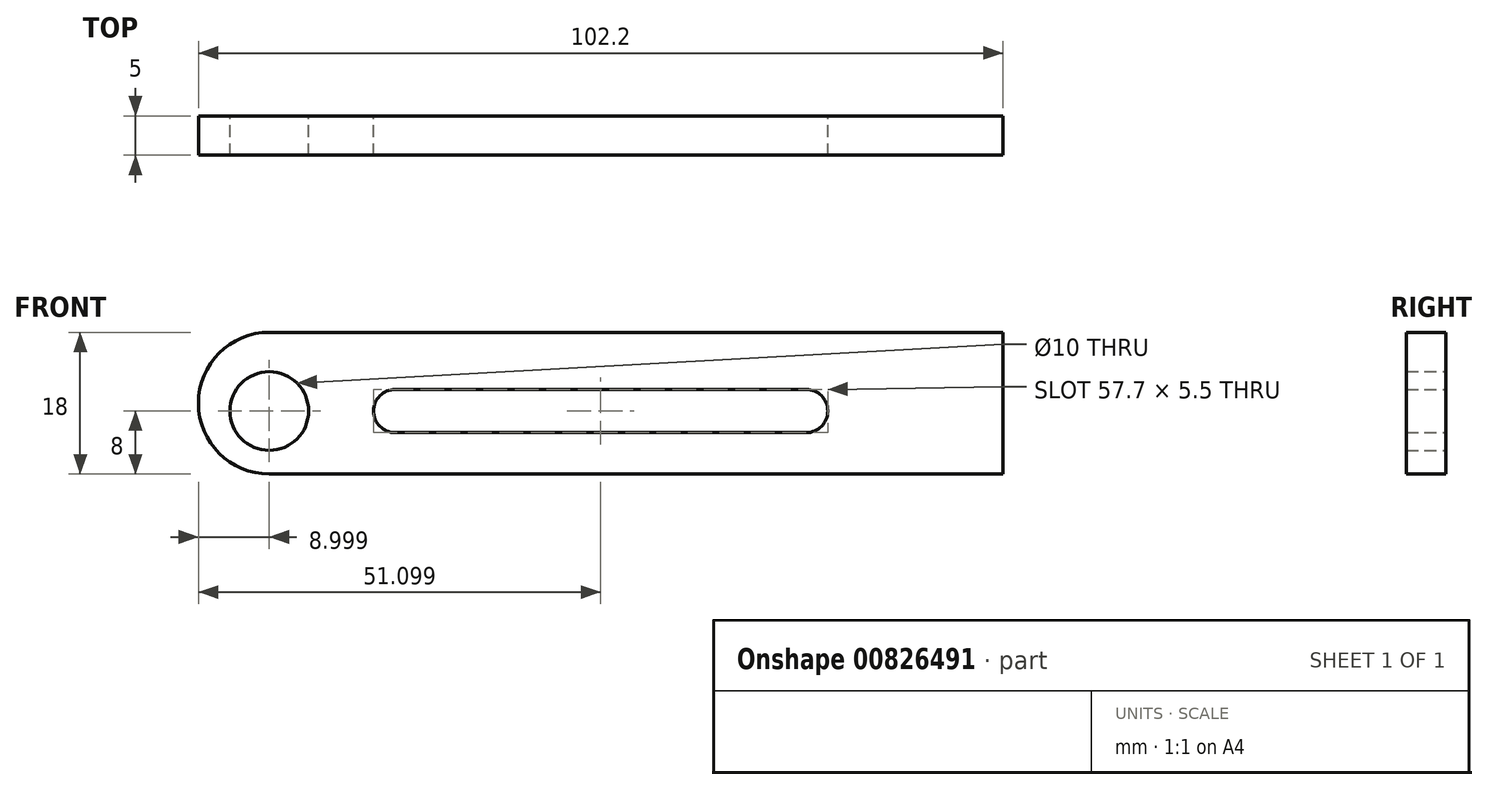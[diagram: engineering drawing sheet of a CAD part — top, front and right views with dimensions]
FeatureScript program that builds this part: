
annotation { "Feature Type Name" : "Feature", "Feature Type Description" : "" }
export const myFeature = defineFeature(function(context is Context, id is Id, definition is map)
    precondition{}
    {
        {
            var Q0;
            Q0=qCreatedBy(makeId("Front.planeOp"),FACE);
            var sketch = newSketch(context, id + "F0", { "sketchPlane" : qUnion([Q0])});
            skCircle(sketch, "E0", {"center": v(-38.63, 0) * mm, "radius": 5 * mm});
            skPoint(sketch, "E1", {"position": v(-22.63, 0) * mm});
            skPoint(sketch, "E2", {"position": v(29.57, 0) * mm});
            skPoint(sketch, "E3.middle", {"position": v(0, 0) * mm});
            skPoint(sketch, "E4", {"position": v(-38.63, 10) * mm});
            skPoint(sketch, "E5", {"position": v(-38.63, -8) * mm});
            skArc(sketch, "E6", {"start": v(-38.63, 10) * mm, "mid": v(-47.63, 1) * mm, "end": v(-38.63, -8) * mm});
            skArc(sketch, "E7", {"start": v(29.57, -2.75) * mm, "mid": v(32.32, 0) * mm, "end": v(29.57, 2.75) * mm});
            skLineSegment(sketch, "E8.right", {"start": v(29.57, -2.75) * mm, "end": v(29.57, -4.4) * mm});
            skLineSegment(sketch, "E9", {"start": v(-22.63, 2.75) * mm, "end": v(29.57, 2.75) * mm});
            skLineSegment(sketch, "E10", {"start": v(-22.63, -2.75) * mm, "end": v(29.57, -2.75) * mm});
            skPoint(sketch, "E11.orphan", {"position": v(29.57, -2.5) * mm});
            skArc(sketch, "E12", {"start": v(-22.63, 2.75) * mm, "mid": v(-25.38, 0) * mm, "end": v(-22.63, -2.75) * mm});
            skLineSegment(sketch, "E13.right", {"start": v(54.57, 10) * mm, "end": v(54.57, -8) * mm});
            skLineSegment(sketch, "E14", {"start": v(-38.63, 10) * mm, "end": v(54.57, 10) * mm});
            skLineSegment(sketch, "E15", {"start": v(-38.63, -8) * mm, "end": v(54.57, -8) * mm});
            skSolve(sketch);
        }
        {
            var Q0;
            Q0=qSketchRegion(id+"F0",true);
            extrude(context, id + "F1", {"entities" : qUnion([Q0]), "depth" : 5 * mm, "offsetDistance" : 25 * mm});
        }
    });
